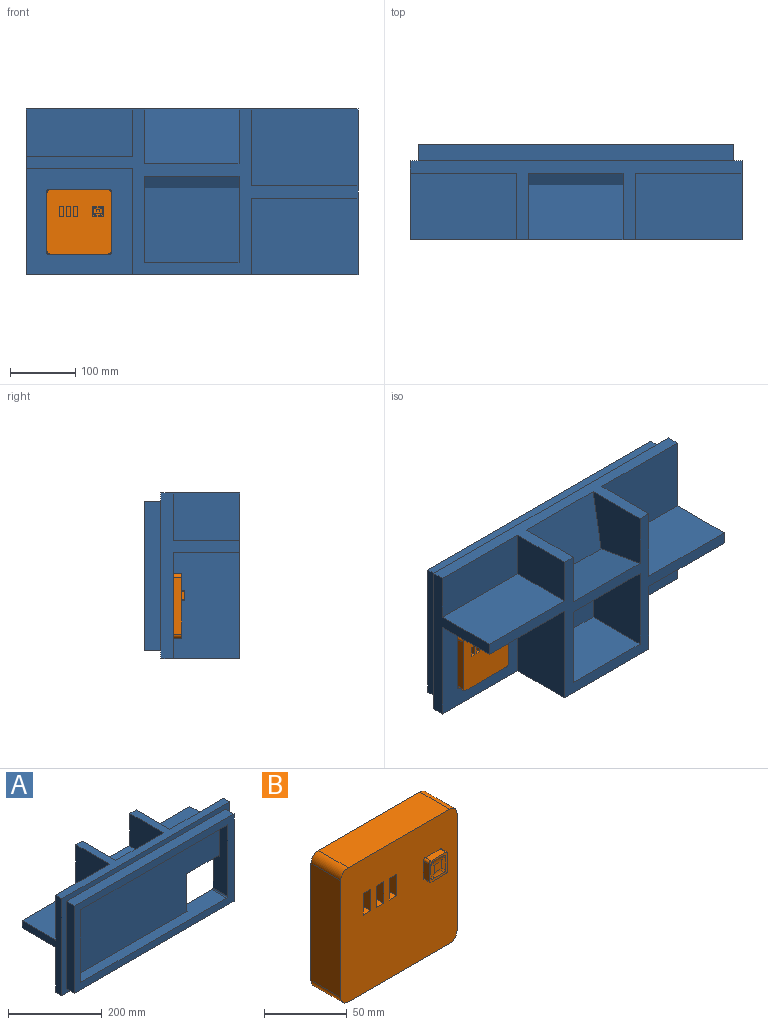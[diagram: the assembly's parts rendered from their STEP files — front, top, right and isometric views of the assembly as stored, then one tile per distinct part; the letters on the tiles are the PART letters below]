
ASSEMBLY  parts=2 mates=1
PART A: 43 faces, bbox 508x146.1x254 mm
  f0: plane 144.31x114.3mm, normal (0,1,0), area 16494.7mm2, adj f2,f24,f25,f38
  f1: plane 101.6x98.54mm, normal (1,0,0), area 8529.9mm2, adj f11,f35,f36,f37
  f2: plane 132.22x101.6mm, normal (-1,0,0), area 12523mm2, adj f0,f25,f35,f38
  f3: plane 163.03x117.48mm, normal (0,1,0), area 19151.9mm2, adj f11,f12,f33,f34
  f4: plane 163.03x117.48mm, normal (0,1,0), area 19151.9mm2, adj f9,f12,f31,f32
  f5: plane 162.56x162.56mm, normal (0,1,0), area 16621.5mm2, adj f9,f10,f17,f20,f22,f23,f29,f30
  f6: plane 162.56x72.39mm, normal (0,1,0), area 11767.7mm2, adj f10,f11,f27,f28
  f7: plane 482.6x228.6mm, normal (0,-1,0), area 25647.3mm2, adj f13,f14,f15,f16,f17,f18,f19,f20
  f8: plane 508x254mm, normal (0,-1,0), area 18709.6mm2, adj f9,f10,f11,f12,f13,f14,f15,f16
  f9: plane 508x120.65mm, normal (0,0,-1), area 28210.3mm2, adj f4,f5,f8,f10,f12,f30,f31,f35
  f10: plane 254x120.65mm, normal (1,0,0), area 6774.2mm2, adj f5,f6,f8,f9,f11,f28,f29,f35
  f11: plane 508x120.65mm, normal (0,0,1), area 13548.4mm2, adj f1,f3,f6,f8,f10,f12,f26,f27
  f12: plane 254x120.65mm, normal (-1,0,0), area 6774.2mm2, adj f3,f4,f8,f9,f11,f32,f33,f35
  f13: plane 228.6x25.4mm, normal (1,0,0), area 5806.4mm2, adj f7,f8,f14,f16
  f14: plane 482.6x25.4mm, normal (0,0,1), area 12258mm2, adj f7,f8,f13,f15
  f15: plane 228.6x25.4mm, normal (-1,0,0), area 5806.4mm2, adj f7,f8,f14,f16
  f16: plane 482.6x25.4mm, normal (0,0,-1), area 12258mm2, adj f7,f8,f13,f15
  f17: plane 187.33x44.45mm, normal (-1,0,0), area 6524.2mm2, adj f5,f7,f18,f21,f39,f42
  f18: plane 444.5x25.4mm, normal (0,0,-1), area 11290.3mm2, adj f7,f17,f19,f21
  f19: plane 190.5x25.4mm, normal (1,0,0), area 4838.7mm2, adj f7,f18,f20,f21
  f20: plane 441.33x44.45mm, normal (0,0,1), area 12975.8mm2, adj f5,f7,f19,f21,f41,f42
  f21: plane 444.5x190.5mm, normal (0,-1,0), area 74870.9mm2, adj f17,f18,f19,f20,f22,f23,f39,f40
  f22: plane 92.71x19.05mm, normal (0,0,-1), area 1766.1mm2, adj f5,f21,f39,f40
  f23: plane 92.71x19.05mm, normal (1,0,0), area 1766.1mm2, adj f5,f21,f40,f41
  f24: plane 132.22x101.6mm, normal (1,0,0), area 12523mm2, adj f0,f25,f35,f38
  f25: plane 144.31x101.6mm, normal (0,0,1), area 14662mm2, adj f0,f2,f24,f35
  f26: plane 101.6x98.54mm, normal (-1,0,0), area 8529.9mm2, adj f11,f35,f36,f37
  f27: plane 101.6x72.39mm, normal (1,0,0), area 7354.8mm2, adj f6,f11,f28,f35
  f28: plane 162.56x101.6mm, normal (0,0,1), area 16516.1mm2, adj f6,f10,f27,f35
  f29: plane 162.56x101.6mm, normal (0,0,-1), area 16516.1mm2, adj f5,f10,f30,f35
  f30: plane 162.56x101.6mm, normal (1,0,0), area 16516.1mm2, adj f5,f9,f29,f35
  f31: plane 117.48x101.6mm, normal (-1,0,0), area 11935.5mm2, adj f4,f9,f32,f35
  f32: plane 163.03x101.6mm, normal (0,0,-1), area 16563.8mm2, adj f4,f12,f31,f35
  f33: plane 163.03x101.6mm, normal (0,0,1), area 16563.8mm2, adj f3,f12,f34,f35
  f34: plane 117.48x101.6mm, normal (-1,0,0), area 11935.5mm2, adj f3,f11,f33,f35
  f35: plane 508x254mm, normal (0,1,0), area 21378.1mm2, adj f1,f2,f9,f10,f11,f12,f24,f25
  f36: plane 144.31x98.54mm, normal (0,0.98,0.17), area 14439.2mm2, adj f1,f11,f26,f37
  f37: plane 144.31x84.23mm, normal (0,-0.17,0.98), area 12342.1mm2, adj f1,f26,f35,f36
  f38: plane 144.31x101.6mm, normal (0,0.17,-0.98), area 14888.2mm2, adj f0,f2,f24,f35
  f39: cylinder r=3.17mm len=19.05mm, axis (0,-1,0), area 95mm2, adj f5,f17,f21,f22
  f40: cylinder r=3.17mm len=19.05mm, axis (0,-1,0), area 95mm2, adj f5,f21,f22,f23
  f41: cylinder r=3.17mm len=19.05mm, axis (0,1,0), area 95mm2, adj f5,f20,f21,f23
  f42: cylinder r=3.17mm len=44.45mm, axis (0,1,0), area 221.7mm2, adj f5,f7,f17,f20
PART B: 43 faces, bbox 99.1x30.2x99.1 mm
  f0: plane 99.06x99.06mm, normal (0,-1,0), area 9226mm2, adj f1,f2,f3,f4,f6,f7,f8,f9
  f1: plane 86.36x25.4mm, normal (0,0,-1), area 2193.5mm2, adj f0,f5,f6,f9
  f2: plane 86.36x25.4mm, normal (1,0,0), area 2193.5mm2, adj f0,f5,f6,f7
  f3: plane 86.36x25.4mm, normal (0,0,1), area 2193.5mm2, adj f0,f5,f7,f8
  f4: plane 86.36x25.4mm, normal (-1,0,0), area 2193.5mm2, adj f0,f5,f8,f9
  f5: plane 99.06x99.06mm, normal (0,1,0), area 9778.3mm2, adj f1,f2,f3,f4,f6,f7,f8,f9
  f6: cylinder r=6.35mm len=25.4mm, axis (0,-1,0), area 253.4mm2, adj f0,f1,f2,f5
  f7: cylinder r=6.35mm len=25.4mm, axis (0,1,0), area 253.4mm2, adj f0,f2,f3,f5
  f8: cylinder r=6.35mm len=25.4mm, axis (0,-1,0), area 253.4mm2, adj f0,f3,f4,f5
  f9: cylinder r=6.35mm len=25.4mm, axis (0,1,0), area 253.4mm2, adj f0,f1,f4,f5
  f10: plane 12.7x4.76mm, normal (-1,0,0), area 60.5mm2, adj f0,f11,f17,f18
  f11: cylinder r=1.59mm len=4.76mm, axis (0,1,0), area 11.9mm2, adj f0,f10,f12,f18
  f12: plane 12.7x4.76mm, normal (0,0,-1), area 60.5mm2, adj f0,f11,f13,f18
  f13: cylinder r=1.59mm len=4.76mm, axis (0,1,0), area 11.9mm2, adj f0,f12,f14,f18
  f14: plane 12.7x4.76mm, normal (1,0,0), area 60.5mm2, adj f0,f13,f15,f18
  f15: cylinder r=1.59mm len=4.76mm, axis (0,1,0), area 11.9mm2, adj f0,f14,f16,f18
  f16: plane 12.7x4.76mm, normal (0,0,1), area 60.5mm2, adj f0,f15,f17,f18
  f17: cylinder r=1.59mm len=4.76mm, axis (0,1,0), area 11.9mm2, adj f0,f10,f16,f18
  f18: plane 15.88x15.88mm, normal (0,-1,0), area 90.7mm2, adj f10,f11,f12,f13,f14,f15,f16,f17
  f19: plane 5.59x5.59mm, normal (0,-1,0), area 31.2mm2, adj f21,f22,f25,f26
  f20: bspline ~3.56x3.56mm, area 5.2mm2, adj f18,f21,f22
  f21: cylinder r=12.7mm len=9.53mm, axis (0,0,-1), area 27.2mm2, adj f18,f19,f20,f23
  f22: cylinder r=12.7mm len=9.53mm, axis (-1,0,0), area 27.2mm2, adj f18,f19,f20,f24
  f23: bspline ~3.56x3.56mm, area 5.2mm2, adj f18,f21,f25
  f24: bspline ~3.56x3.56mm, area 5.2mm2, adj f18,f22,f26
  f25: cylinder r=12.7mm len=9.53mm, axis (-1,0,0), area 27.2mm2, adj f18,f19,f23,f27
  f26: cylinder r=12.7mm len=9.53mm, axis (0,0,-1), area 27.2mm2, adj f18,f19,f24,f27
  f27: bspline ~3.56x3.56mm, area 5.2mm2, adj f18,f25,f26
  f28: plane 12.7x6.35mm, normal (0,0,1), area 80.6mm2, adj f0,f29,f31,f32
  f29: plane 15.88x12.7mm, normal (-1,0,0), area 201.6mm2, adj f0,f28,f30,f32
  f30: plane 12.7x6.35mm, normal (0,0,-1), area 80.6mm2, adj f0,f29,f31,f32
  f31: plane 15.88x12.7mm, normal (1,0,0), area 201.6mm2, adj f0,f28,f30,f32
  f32: plane 15.88x6.35mm, normal (0,-1,0), area 100.8mm2, adj f28,f29,f30,f31
  f33: plane 12.7x6.35mm, normal (0,0,1), area 80.6mm2, adj f0,f34,f36,f37
  f34: plane 15.88x12.7mm, normal (-1,0,0), area 201.6mm2, adj f0,f33,f35,f37
  f35: plane 12.7x6.35mm, normal (0,0,-1), area 80.6mm2, adj f0,f34,f36,f37
  f36: plane 15.88x12.7mm, normal (1,0,0), area 201.6mm2, adj f0,f33,f35,f37
  f37: plane 15.88x6.35mm, normal (0,-1,0), area 100.8mm2, adj f33,f34,f35,f36
  f38: plane 15.88x12.7mm, normal (-1,0,0), area 201.6mm2, adj f0,f39,f41,f42
  f39: plane 12.7x6.35mm, normal (0,0,-1), area 80.6mm2, adj f0,f38,f40,f42
  f40: plane 15.88x12.7mm, normal (1,0,0), area 201.6mm2, adj f0,f39,f41,f42
  f41: plane 12.7x6.35mm, normal (0,0,1), area 80.6mm2, adj f0,f38,f40,f42
  f42: plane 15.88x6.35mm, normal (0,-1,0), area 100.8mm2, adj f38,f39,f40,f41
PLACE A rot(axis=(0,0,1),180deg) t=(179.2,-84.11,6.57)mm
PLACE B t=(6.48,-71.41,-39.15)mm
MATE planar A.f17 <-> B.f4  axis (1,0,0) through (-43.05,-84.11,-39.15)mm
